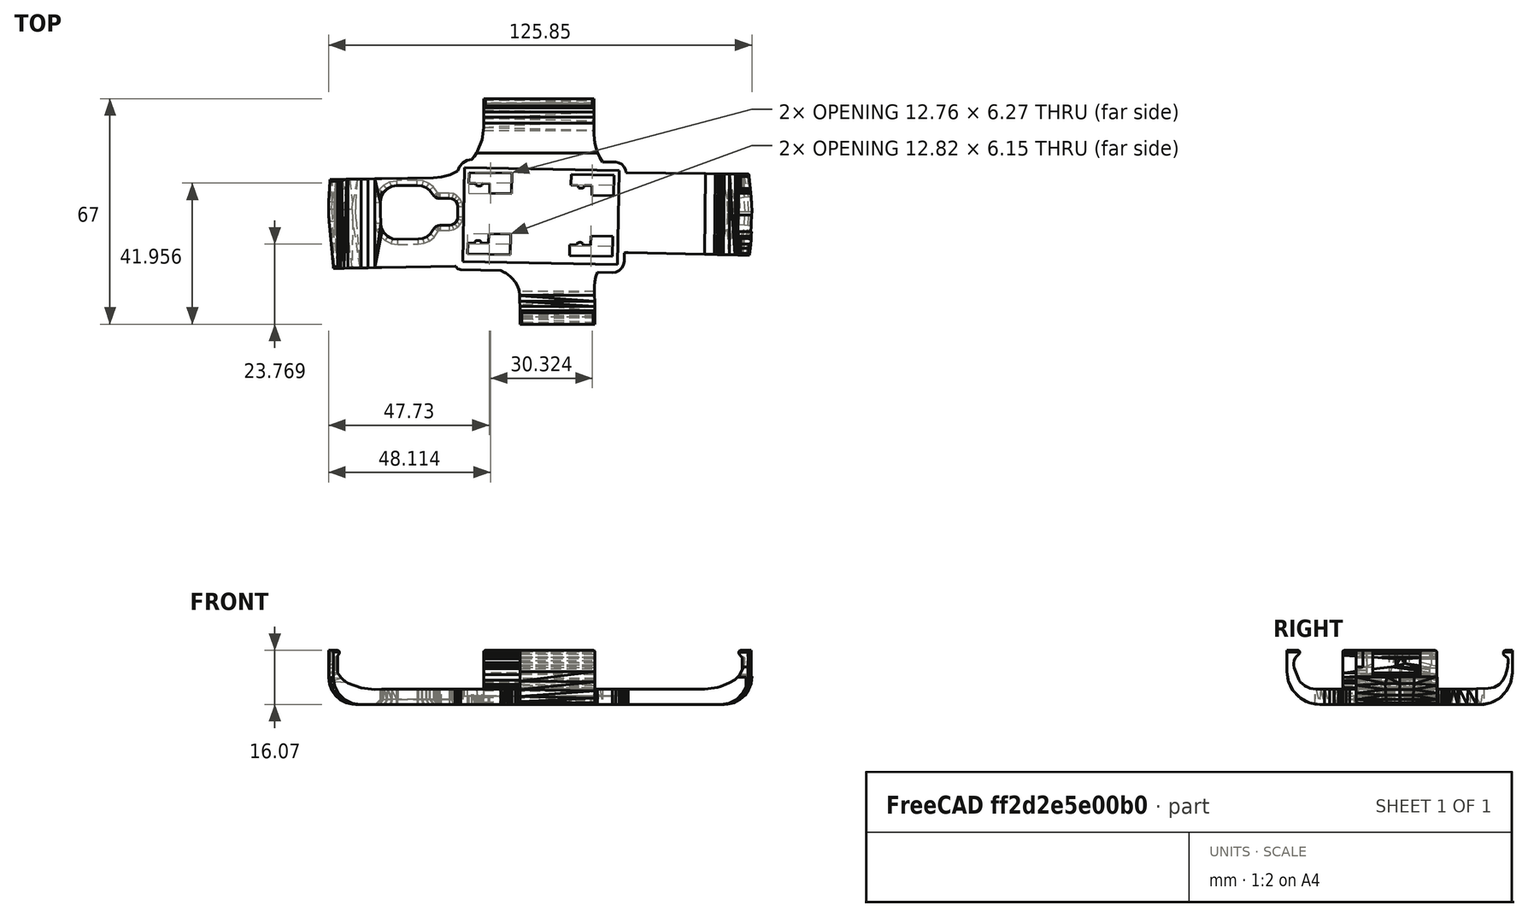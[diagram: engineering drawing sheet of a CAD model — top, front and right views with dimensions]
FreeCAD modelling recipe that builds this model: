
FCSTD DOCUMENT  (FreeCAD 0.18R16110 (Git))
Label: s3
License: All rights reserved
LicenseURL: http://en.wikipedia.org/wiki/All_rights_reserved
objects: Part::Box×5, Part::Feature×5, Part::Cut×5, Part::MultiFuse×1
note: 16 computed .brp shape members not serialized (recipe doc carries the construction recipe); baked Part::Feature solids carry a one-line shape summary decoded from their .brp

FEATURE [Part::Box] Box002  label="Cube002"
  AttacherType = Attacher::AttachEngine3D
  Height = 20
  Length = 20
  Placement = pos=(76,7.39,4.1) rot=(0,0,1;0rad)
  Width = 7
FEATURE [Part::Feature] to_be_fixed001_solid001001  label="to_be_fixed001 (Solid)002"
  shape: bbox 125.8 x 67 x 16.07 mm, 1129 faces (baked)
FEATURE [Part::Feature] Common002
  Placement = pos=(0,-3.66,0) rot=(0,0,1;0rad)
  shape: bbox 4.136 x 10.57 x 7.9 mm, 145 faces (baked)
FEATURE [Part::Cut] Cut
  Base = -> to_be_fixed001_solid001001
  Tool = -> Box002
FEATURE [Part::MultiFuse] Fusion
  Shapes = -> [Cut,Common002]
FEATURE [Part::Box] Box003  label="Cube003"
  AttacherType = Attacher::AttachEngine3D
  Height = 20
  Length = 20
  Placement = pos=(76,-4.56,1.1) rot=(0,0,1;0rad)
  Width = 7
FEATURE [Part::Cut] Cut001
  Base = -> Fusion
  Tool = -> Box003
FEATURE [Part::Feature] Common003
  Placement = pos=(0,-3.66,27) rot=(0,0,1;0rad)
  shape: bbox 4.136 x 10.57 x 7.9 mm, 145 faces (baked)
FEATURE [Part::Box] Box  label="Cube"
  AttacherType = Attacher::AttachEngine3D
  Height = 10
  Length = 10
  Placement = pos=(82,-5,8) rot=(0,0,1;0rad)
  Width = 10
FEATURE [Part::Box] Box004  label="Cube004"
  AttacherType = Attacher::AttachEngine3D
  Height = 10
  Length = 10
  Placement = pos=(82,2,30) rot=(0,0,1;0rad)
  Width = 10
FEATURE [Part::Cut] Cut002
  Base = -> Common003
  Tool = -> Box
FEATURE [Part::Cut] Cut003
  Base = -> Cut002
  Placement = pos=(0,3.67,-27) rot=(0,0,1;0rad)
  Tool = -> Box004
FEATURE [Part::Box] Box005  label="Cube005"
  AttacherType = Attacher::AttachEngine3D
  Height = 20
  Length = 20
  Placement = pos=(76,-2.56,7.1) rot=(0,0,1;0rad)
  Width = 7
FEATURE [Part::Cut] Cut004
  Base = -> Cut001
  Tool = -> Box005
FEATURE [Part::Feature] Cut003001  label="Cut005"
  Placement = pos=(0,3.67,-27) rot=(0,0,1;0rad)
  shape: bbox 3.447 x 3.233 x 7.9 mm, 82 faces (baked)
FEATURE [Part::Feature] Cut004001  label="Cut006"
  shape: bbox 125.8 x 67 x 16.07 mm, 1180 faces (baked)
